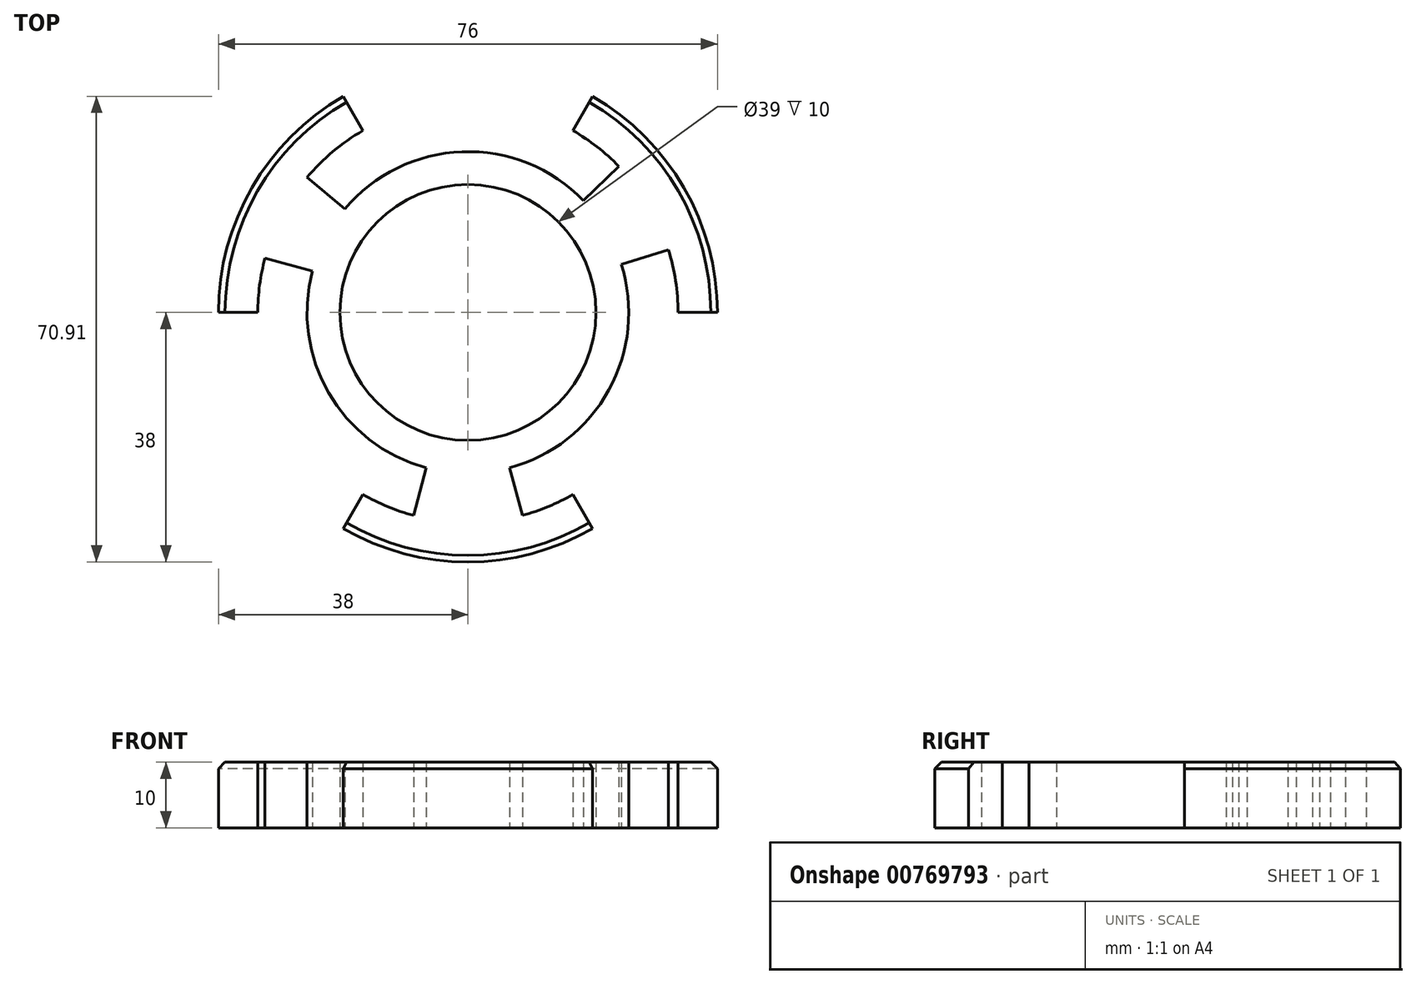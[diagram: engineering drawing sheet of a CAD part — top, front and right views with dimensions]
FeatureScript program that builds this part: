
annotation { "Feature Type Name" : "Feature", "Feature Type Description" : "" }
export const myFeature = defineFeature(function(context is Context, id is Id, definition is map)
    precondition{}
    {
        {
            var Q0;
            Q0=qCreatedBy(makeId("Top.planeOp"),FACE);
            var sketch = newSketch(context, id + "F0", { "sketchPlane" : qUnion([Q0])});
            skCircle(sketch, "E0", {"center": v(0, 0) * mm, "radius": 19.5 * mm});
            skCircle(sketch, "E1", {"center": v(0, 0) * mm, "radius": 38 * mm});
            skLineSegment(sketch, "E2", {"start": v(0, 0) * mm, "end": v(0, -48.72) * mm, "construction": true});
            skCircle(sketch, "E3", {"center": v(0, 0) * mm, "radius": 32 * mm});
            skLineSegment(sketch, "E4", {"start": v(-24.14, 0) * mm, "end": v(-50.37, 0) * mm});
            skLineSegment(sketch, "E5.MirrorCS", {"start": v(-12.07, 20.9) * mm, "end": v(-25.19, 43.62) * mm});
            skLineSegment(sketch, "E6", {"start": v(0, 0) * mm, "end": v(-31.46, 8.43) * mm});
            skLineSegment(sketch, "E7.MirrorCS", {"start": v(0, 0) * mm, "end": v(-24.95, 20.94) * mm});
            skLineSegment(sketch, "E8", {"start": v(0, 0) * mm, "end": v(24.14, 23.38) * mm});
            skLineSegment(sketch, "E9", {"start": v(0, 0) * mm, "end": v(46.5, 0) * mm});
            skLineSegment(sketch, "E10.MirrorCS", {"start": v(0, 0) * mm, "end": v(32.33, 10.12) * mm});
            skLineSegment(sketch, "E11.MirrorCS", {"start": v(0, 0) * mm, "end": v(23.25, 40.27) * mm});
            skLineSegment(sketch, "E12", {"start": v(0, 0) * mm, "end": v(-8.44, -31.51) * mm});
            skLineSegment(sketch, "E13.MirrorCS", {"start": v(0, 0) * mm, "end": v(8.44, -31.51) * mm});
            skLineSegment(sketch, "E14", {"start": v(0, 0) * mm, "end": v(-22.66, -39.25) * mm});
            skLineSegment(sketch, "E15.MirrorCS", {"start": v(0, 0) * mm, "end": v(22.66, -39.25) * mm});
            skCircle(sketch, "E16", {"center": v(0, 0) * mm, "radius": 24.5 * mm});
            skSolve(sketch);
        }
        {
            var Q0;
            {var subQ0=sQuery(id+"F0.wireOp",EDGE,"E10.MirrorCS");var subQ1=sQuery(id+"F0.wireOp",EDGE,"E3");var subQ2=makeQuery(id+"F0.imprint","INTERSECT",VERTEX,{"derivedFrom":[subQ1,subQ0]});Q0=makeQuery(id+"F0.imprint","IMPRINT",FACE,{"disambiguationData":[TD([[makeQuery(id+"F0.imprint","IMPRINT",EDGE,{"disambiguationData":[TD([[subQ2,-1.0]])],"derivedFrom":subQ1}),1.0]])]});}
            var Q1;
            {var subQ0=sQuery(id+"F0.wireOp",EDGE,"E6");var subQ1=sQuery(id+"F0.wireOp",EDGE,"E0");var subQ2=makeQuery(id+"F0.imprint","INTERSECT",VERTEX,{"derivedFrom":[subQ1,subQ0]});Q1=makeQuery(id+"F0.imprint","IMPRINT",FACE,{"disambiguationData":[TD([[makeQuery(id+"F0.imprint","IMPRINT",EDGE,{"disambiguationData":[TD([[subQ2,-1.0]])],"derivedFrom":subQ1}),-1.0]])]});}
            var Q2;
            {var subQ0=sQuery(id+"F0.wireOp",EDGE,"E7.MirrorCS");var subQ1=sQuery(id+"F0.wireOp",EDGE,"E0");var subQ2=makeQuery(id+"F0.imprint","INTERSECT",VERTEX,{"derivedFrom":[subQ1,subQ0]});Q2=makeQuery(id+"F0.imprint","IMPRINT",FACE,{"disambiguationData":[TD([[makeQuery(id+"F0.imprint","IMPRINT",EDGE,{"disambiguationData":[TD([[subQ2,-1.0]])],"derivedFrom":subQ1}),-1.0]])]});}
            var Q3;
            {var subQ0=sQuery(id+"F0.wireOp",EDGE,"E11.MirrorCS");var subQ1=sQuery(id+"F0.wireOp",EDGE,"E0");var subQ2=makeQuery(id+"F0.imprint","INTERSECT",VERTEX,{"derivedFrom":[subQ1,subQ0]});Q3=makeQuery(id+"F0.imprint","IMPRINT",FACE,{"disambiguationData":[TD([[makeQuery(id+"F0.imprint","IMPRINT",EDGE,{"disambiguationData":[TD([[subQ2,-1.0]])],"derivedFrom":subQ1}),-1.0]])]});}
            var Q4;
            {var subQ0=sQuery(id+"F0.wireOp",EDGE,"E8");var subQ1=sQuery(id+"F0.wireOp",EDGE,"E0");var subQ2=makeQuery(id+"F0.imprint","INTERSECT",VERTEX,{"derivedFrom":[subQ1,subQ0]});Q4=makeQuery(id+"F0.imprint","IMPRINT",FACE,{"disambiguationData":[TD([[makeQuery(id+"F0.imprint","IMPRINT",EDGE,{"disambiguationData":[TD([[subQ2,-1.0]])],"derivedFrom":subQ1}),-1.0]])]});}
            var Q5;
            {var subQ0=sQuery(id+"F0.wireOp",EDGE,"E7.MirrorCS");var subQ1=sQuery(id+"F0.wireOp",EDGE,"E3");var subQ2=makeQuery(id+"F0.imprint","INTERSECT",VERTEX,{"derivedFrom":[subQ1,subQ0]});Q5=makeQuery(id+"F0.imprint","IMPRINT",FACE,{"disambiguationData":[TD([[makeQuery(id+"F0.imprint","IMPRINT",EDGE,{"disambiguationData":[TD([[subQ2,-1.0]])],"derivedFrom":subQ1}),1.0]])]});}
            var Q6;
            {var subQ0=sQuery(id+"F0.wireOp",EDGE,"E13.MirrorCS");var subQ1=sQuery(id+"F0.wireOp",EDGE,"E0");var subQ2=makeQuery(id+"F0.imprint","INTERSECT",VERTEX,{"derivedFrom":[subQ1,subQ0]});Q6=makeQuery(id+"F0.imprint","IMPRINT",FACE,{"disambiguationData":[TD([[makeQuery(id+"F0.imprint","IMPRINT",EDGE,{"disambiguationData":[TD([[subQ2,-1.0]])],"derivedFrom":subQ1}),-1.0]])]});}
            var Q7;
            {var subQ0=sQuery(id+"F0.wireOp",EDGE,"E9");var subQ1=sQuery(id+"F0.wireOp",EDGE,"E0");var subQ2=makeQuery(id+"F0.imprint","INTERSECT",VERTEX,{"derivedFrom":[subQ1,subQ0]});Q7=makeQuery(id+"F0.imprint","IMPRINT",FACE,{"disambiguationData":[TD([[makeQuery(id+"F0.imprint","IMPRINT",EDGE,{"disambiguationData":[TD([[subQ2,1.0]])],"derivedFrom":subQ1}),-1.0]])]});}
            var Q8;
            {var subQ0=sQuery(id+"F0.wireOp",EDGE,"E10.MirrorCS");var subQ1=sQuery(id+"F0.wireOp",EDGE,"E0");var subQ2=makeQuery(id+"F0.imprint","INTERSECT",VERTEX,{"derivedFrom":[subQ1,subQ0]});Q8=makeQuery(id+"F0.imprint","IMPRINT",FACE,{"disambiguationData":[TD([[makeQuery(id+"F0.imprint","IMPRINT",EDGE,{"disambiguationData":[TD([[subQ2,-1.0]])],"derivedFrom":subQ1}),-1.0]])]});}
            var Q9;
            {var subQ0=sQuery(id+"F0.wireOp",EDGE,"E12");var subQ1=sQuery(id+"F0.wireOp",EDGE,"E0");var subQ2=makeQuery(id+"F0.imprint","INTERSECT",VERTEX,{"derivedFrom":[subQ1,subQ0]});Q9=makeQuery(id+"F0.imprint","IMPRINT",FACE,{"disambiguationData":[TD([[makeQuery(id+"F0.imprint","IMPRINT",EDGE,{"disambiguationData":[TD([[subQ2,-1.0]])],"derivedFrom":subQ1}),-1.0]])]});}
            var Q10;
            {var subQ0=sQuery(id+"F0.wireOp",EDGE,"E14");var subQ1=sQuery(id+"F0.wireOp",EDGE,"E0");var subQ2=makeQuery(id+"F0.imprint","INTERSECT",VERTEX,{"derivedFrom":[subQ1,subQ0]});Q10=makeQuery(id+"F0.imprint","IMPRINT",FACE,{"disambiguationData":[TD([[makeQuery(id+"F0.imprint","IMPRINT",EDGE,{"disambiguationData":[TD([[subQ2,-1.0]])],"derivedFrom":subQ1}),-1.0]])]});}
            var Q11;
            {var subQ0=sQuery(id+"F0.wireOp",EDGE,"E10.MirrorCS");var subQ1=sQuery(id+"F0.wireOp",EDGE,"E0");var subQ2=makeQuery(id+"F0.imprint","INTERSECT",VERTEX,{"derivedFrom":[subQ1,subQ0]});Q11=makeQuery(id+"F0.imprint","IMPRINT",FACE,{"disambiguationData":[TD([[makeQuery(id+"F0.imprint","IMPRINT",EDGE,{"disambiguationData":[TD([[subQ2,1.0]])],"derivedFrom":subQ1}),-1.0]])]});}
            var Q12;
            {var subQ2=sQuery(id+"F0.wireOp",EDGE,"E11.MirrorCS");var subQ7=sQuery(id+"F0.wireOp",EDGE,"E1");var subQ8=makeQuery(id+"F0.imprint","INTERSECT",VERTEX,{"derivedFrom":[subQ7,subQ2]});Q12=makeQuery(id+"F0.imprint","IMPRINT",FACE,{"disambiguationData":[TD([[makeQuery(id+"F0.imprint","IMPRINT",EDGE,{"disambiguationData":[TD([[subQ8,1.0]])],"derivedFrom":subQ7}),1.0]])]});}
            var Q13;
            {var subQ3=sQuery(id+"F0.wireOp",EDGE,"E5.MirrorCS");var subQ7=sQuery(id+"F0.wireOp",EDGE,"E1");var subQ8=makeQuery(id+"F0.imprint","INTERSECT",VERTEX,{"derivedFrom":[subQ7,subQ3]});Q13=makeQuery(id+"F0.imprint","IMPRINT",FACE,{"disambiguationData":[TD([[makeQuery(id+"F0.imprint","IMPRINT",EDGE,{"disambiguationData":[TD([[subQ8,-1.0]])],"derivedFrom":subQ7}),1.0]])]});}
            var Q14;
            {var subQ4=sQuery(id+"F0.wireOp",EDGE,"E14");var subQ5=sQuery(id+"F0.wireOp",EDGE,"E1");var subQ6=makeQuery(id+"F0.imprint","INTERSECT",VERTEX,{"derivedFrom":[subQ5,subQ4]});Q14=makeQuery(id+"F0.imprint","IMPRINT",FACE,{"disambiguationData":[TD([[makeQuery(id+"F0.imprint","IMPRINT",EDGE,{"disambiguationData":[TD([[subQ6,-1.0]])],"derivedFrom":subQ5}),1.0]])]});}
            var Q15;
            {var subQ0=sQuery(id+"F0.wireOp",EDGE,"E12");var subQ1=sQuery(id+"F0.wireOp",EDGE,"E3");var subQ2=makeQuery(id+"F0.imprint","INTERSECT",VERTEX,{"derivedFrom":[subQ1,subQ0]});Q15=makeQuery(id+"F0.imprint","IMPRINT",FACE,{"disambiguationData":[TD([[makeQuery(id+"F0.imprint","IMPRINT",EDGE,{"disambiguationData":[TD([[subQ2,-1.0]])],"derivedFrom":subQ1}),1.0]])]});}
            extrude(context, id + "F1", {"entities" : qUnion([Q0, Q1, Q2, Q3, Q4, Q5, Q6, Q7, Q8, Q9, Q10, Q11, Q12, Q13, Q14, Q15]), "depth" : 10 * mm, "offsetDistance" : 25 * mm});
        }
        {
            var Q0;
            {var subQ0=sQuery(id+"F0.wireOp",EDGE,"E1");Q0=makeQuery(id+"F1.opExtrude","CAP_EDGE",EDGE,{"disambiguationData":[OSD([subQ0]),TDD([makeQuery(id+"F0.imprint","IMPRINT",EDGE,{"disambiguationData":[TD([[makeQuery(id+"F0.imprint","INTERSECT",VERTEX,{"derivedFrom":[subQ0,sQuery(id+"F0.wireOp",EDGE,"E11.MirrorCS")]}),1.0]])],"derivedFrom":subQ0})])],"isStart":false});}
            var Q1;
            {var subQ0=sQuery(id+"F0.wireOp",EDGE,"E1");Q1=makeQuery(id+"F1.opExtrude","CAP_EDGE",EDGE,{"disambiguationData":[OSD([subQ0]),TDD([makeQuery(id+"F0.imprint","IMPRINT",EDGE,{"disambiguationData":[TD([[makeQuery(id+"F0.imprint","INTERSECT",VERTEX,{"derivedFrom":[subQ0,sQuery(id+"F0.wireOp",EDGE,"E5.MirrorCS")]}),-1.0]])],"derivedFrom":subQ0})])],"isStart":false});}
            var Q2;
            {var subQ0=sQuery(id+"F0.wireOp",EDGE,"E1");Q2=makeQuery(id+"F1.opExtrude","CAP_EDGE",EDGE,{"disambiguationData":[OSD([subQ0]),TDD([makeQuery(id+"F0.imprint","IMPRINT",EDGE,{"disambiguationData":[TD([[makeQuery(id+"F0.imprint","INTERSECT",VERTEX,{"derivedFrom":[subQ0,sQuery(id+"F0.wireOp",EDGE,"E14")]}),-1.0]])],"derivedFrom":subQ0})])],"isStart":false});}
            chamfer(context, id + "F2", {"entities" : qUnion([Q0, Q1, Q2]), "width" : 1 * mm, "tangentPropagation" : true});
        }
    });
